FCSTD DOCUMENT  (FreeCAD 0.21R33771 (Git))
Label: pcb_layout
License: All rights reserved
LicenseURL: http://en.wikipedia.org/wiki/All_rights_reserved
objects: Sketcher::SketchObject×1, PartDesign::Body×1
note: 2 computed .brp shape members not serialized (recipe doc carries the construction recipe); baked Part::Feature solids carry a one-line shape summary decoded from their .brp

FEATURE [Sketcher::SketchObject] Sketch
  FullyConstrained = true
  MapMode = 5
  Support = -> [XY_Plane]
  expr: Constraints[56] = .Constraints.d1 / 2
  sketch-geometry (23):
    g0: LineSegment StartX=4.17e-14 StartY=6.111e-13 StartZ=0 EndX=70 EndY=1.2266e-12 EndZ=0
    g1: LineSegment StartX=70 StartY=1.2266e-12 StartZ=0 EndX=70 EndY=75 EndZ=0
    g2: LineSegment StartX=70 StartY=75 StartZ=0 EndX=6.679e-13 EndY=75 EndZ=0
    g3: LineSegment StartX=6.679e-13 StartY=75 StartZ=0 EndX=4.17e-14 EndY=6.111e-13 EndZ=0
    g4: Circle CenterX=5 CenterY=70 CenterZ=0 NormalX=0 NormalY=0 NormalZ=1 AngleXU=0 Radius=1.55
    g5: Circle CenterX=65 CenterY=70 CenterZ=0 NormalX=0 NormalY=0 NormalZ=1 AngleXU=0 Radius=1.55
    g6: Circle CenterX=5 CenterY=5 CenterZ=0 NormalX=0 NormalY=0 NormalZ=1 AngleXU=0 Radius=1.55
    g7: Circle CenterX=65 CenterY=5 CenterZ=0 NormalX=0 NormalY=0 NormalZ=1 AngleXU=0 Radius=1.55
    g8: LineSegment StartX=5 StartY=70 StartZ=0 EndX=65 EndY=70 EndZ=0
    g9: LineSegment StartX=65 StartY=70 StartZ=0 EndX=65 EndY=5 EndZ=0
    g10: LineSegment StartX=65 StartY=5 StartZ=0 EndX=5 EndY=5 EndZ=0
    g11: LineSegment StartX=5 StartY=5 StartZ=0 EndX=5 EndY=70 EndZ=0
    g12: LineSegment StartX=6.679e-13 StartY=75 StartZ=0 EndX=5 EndY=75 EndZ=0
    g13: LineSegment StartX=5 StartY=75 StartZ=0 EndX=5 EndY=70 EndZ=0
    g14: LineSegment StartX=5 StartY=70 StartZ=0 EndX=6.679e-13 EndY=70 EndZ=0
    g15: LineSegment StartX=6.679e-13 StartY=70 StartZ=0 EndX=6.679e-13 EndY=75 EndZ=0
    g16: LineSegment StartX=65 StartY=5 StartZ=0 EndX=70 EndY=5 EndZ=0
    g17: LineSegment StartX=70 StartY=5 StartZ=0 EndX=70 EndY=1.2266e-12 EndZ=0
    g18: LineSegment StartX=70 StartY=1.2266e-12 StartZ=0 EndX=65 EndY=1.2266e-12 EndZ=0
    g19: LineSegment StartX=65 StartY=1.2266e-12 StartZ=0 EndX=65 EndY=5 EndZ=0
    g20: Circle CenterX=5 CenterY=35 CenterZ=0 NormalX=0 NormalY=0 NormalZ=1 AngleXU=0 Radius=1.55
    g21: Circle CenterX=65 CenterY=35 CenterZ=0 NormalX=0 NormalY=0 NormalZ=1 AngleXU=0 Radius=1.55
    g22: LineSegment StartX=5 StartY=35 StartZ=0 EndX=65 EndY=35 EndZ=0
  constraints (58):
    c: Horizontal(g2)
    c: Tangent(g0,g-1)
    c: Tangent(g3,g-2)
    c: Distance(g0,g2) = 75  'heigth'
    c: Distance(g1,g3) = 70  'width'
    c: Coincident(g2,g3)
    c: Coincident(g1,g2)
    c: Coincident(g3,g0)
    c: Coincident(g0,g1)
    c: Perpendicular(g1,g0)
    c: Coincident(g8,g9)
    c: Coincident(g9,g10)
    c: Coincident(g10,g11)
    c: Coincident(g11,g8)
    c: Horizontal(g8)
    c: Horizontal(g10)
    c: Vertical(g9)
    c: Vertical(g11)
    c: Coincident(g8,g4)
    c: Coincident(g5,g8)
    c: Coincident(g10,g6)
    c: Coincident(g9,g7)
    c: Coincident(g12,g13)
    c: Coincident(g13,g14)
    c: Coincident(g14,g15)
    c: Coincident(g15,g12)
    c: Horizontal(g12)
    c: Horizontal(g14)
    c: Vertical(g13)
    c: Vertical(g15)
    c: Coincident(g12,g2)
    c: Coincident(g13,g4)
    c: Coincident(g16,g17)
    c: Coincident(g17,g18)
    c: Coincident(g18,g19)
    c: Coincident(g19,g16)
    c: Horizontal(g16)
    c: Horizontal(g18)
    c: Vertical(g17)
    c: Vertical(g19)
    c: Coincident(g16,g7)
    c: Coincident(g17,g0)
    c: Equal(g16,g19)
    c: Equal(g13,g14)
    c: Diameter(g5) = 3.1
    c: Diameter(g4) = 3.1
    c: Equal(g4,g6)
    c: Equal(g6,g7)
    c: Distance(g8) = 60  'd1'
    c: Equal(g5,g21) = 3.1
    c: Equal(g4,g20) = 3.1
    c: Coincident(g22,g20)
    c: Coincident(g22,g21)
    c: Horizontal(g22)
    c: Equal(g22,g10)
    c: PointOnObject(g21,g9)
    c: Distance(g20,g6) = 30
    c: Equal(g19,g13)
FEATURE [PartDesign::Body] Body
  Group = -> [Sketch]
  Origin = -> Origin
